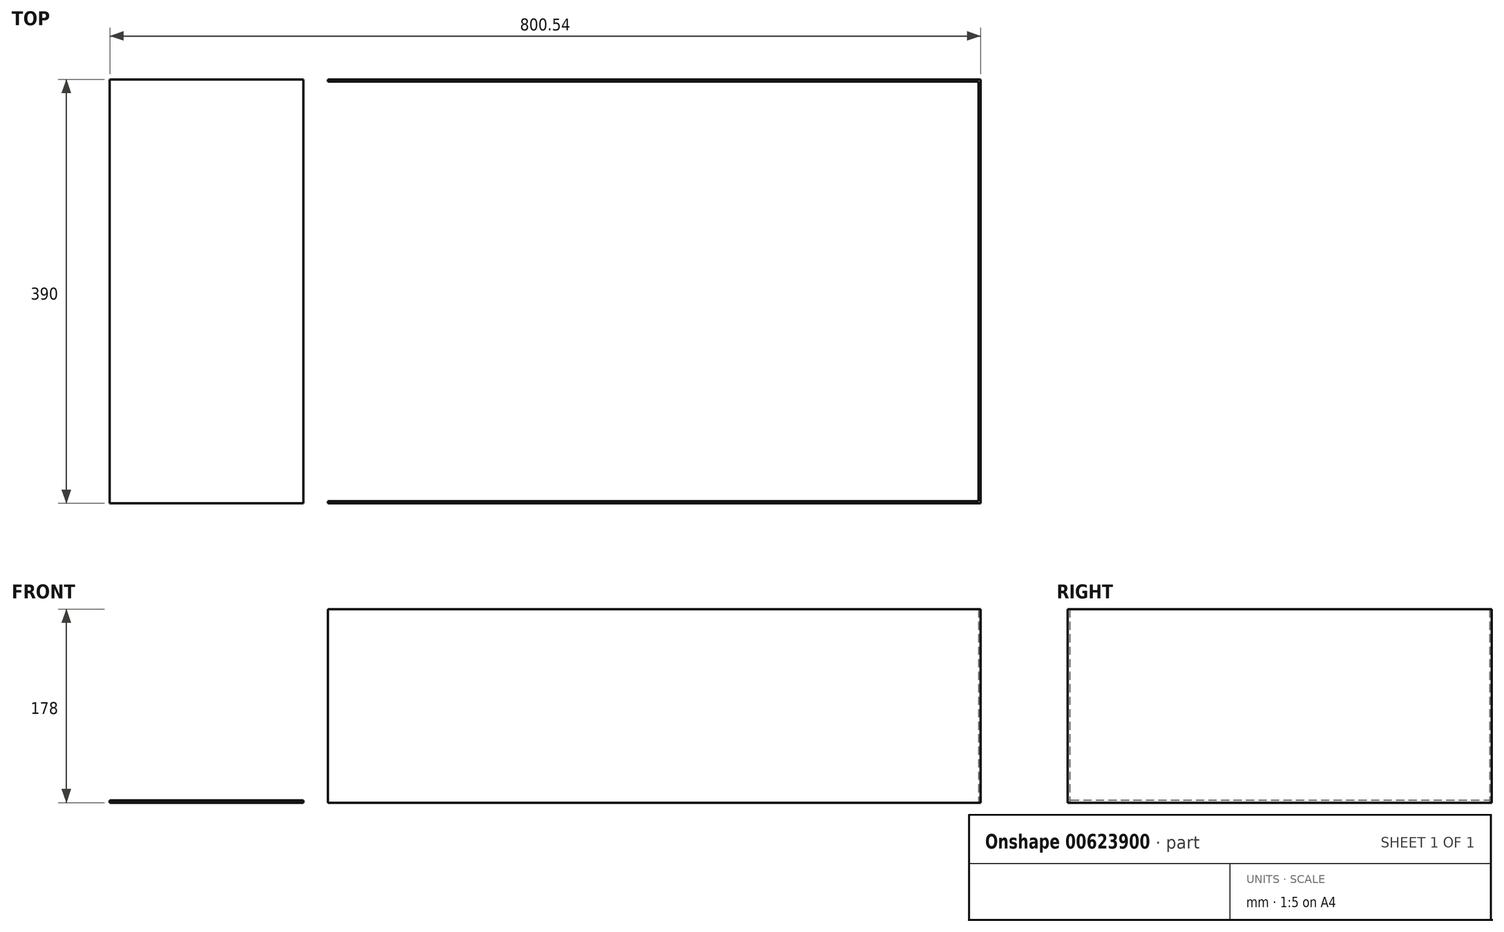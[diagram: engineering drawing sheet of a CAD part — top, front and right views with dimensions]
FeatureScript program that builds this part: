
annotation { "Feature Type Name" : "Feature", "Feature Type Description" : "" }
export const myFeature = defineFeature(function(context is Context, id is Id, definition is map)
    precondition{}
    {
        {
            var Q0;
            Q0=qCreatedBy(makeId("Top.planeOp"),FACE);
            var sketch = newSketch(context, id + "F0", { "sketchPlane" : qUnion([Q0])});
            skLineSegment(sketch, "E0", {"start": v(0, 0) * mm, "end": v(600, 0) * mm});
            skLineSegment(sketch, "E1", {"start": v(600, 0) * mm, "end": v(600, -390) * mm});
            skLineSegment(sketch, "E2", {"start": v(600, -390) * mm, "end": v(0, -390) * mm});
            skLineSegment(sketch, "E3", {"start": v(0, -390) * mm, "end": v(0, -388) * mm});
            skLineSegment(sketch, "E4", {"start": v(0, -388) * mm, "end": v(598, -388) * mm});
            skLineSegment(sketch, "E5", {"start": v(598, -388) * mm, "end": v(598, -2) * mm});
            skLineSegment(sketch, "E6", {"start": v(598, -2) * mm, "end": v(0, -2) * mm});
            skLineSegment(sketch, "E7", {"start": v(0, -2) * mm, "end": v(0, 0) * mm});
            skSolve(sketch);
        }
        {
            var Q0;
            Q0 = qSketchRegion(id + "F0", true);
            extrude(context, id + "F1", {"entities" : qUnion([Q0]), "depth" : 178 * mm, "offsetDistance" : 25 * mm});
        }
        {
            var Q0;
            Q0=qCreatedBy(makeId("Top.planeOp"),FACE);
            var sketch = newSketch(context, id + "F2", { "sketchPlane" : qUnion([Q0])});
            skLineSegment(sketch, "E8.bottom", {"start": v(-22.54, 0) * mm, "end": v(-200.54, 0) * mm});
            skLineSegment(sketch, "E8.top", {"start": v(-22.54, -390) * mm, "end": v(-200.54, -390) * mm});
            skLineSegment(sketch, "E8.left", {"start": v(-22.54, 0) * mm, "end": v(-22.54, -390) * mm});
            skLineSegment(sketch, "E8.right", {"start": v(-200.54, 0) * mm, "end": v(-200.54, -390) * mm});
            skSolve(sketch);
        }
        {
            var Q0;
            Q0 = qSketchRegion(id + "F2", true);
            extrude(context, id + "F3", {"entities" : qUnion([Q0]), "depth" : 2 * mm, "offsetDistance" : 25 * mm});
        }
    });
